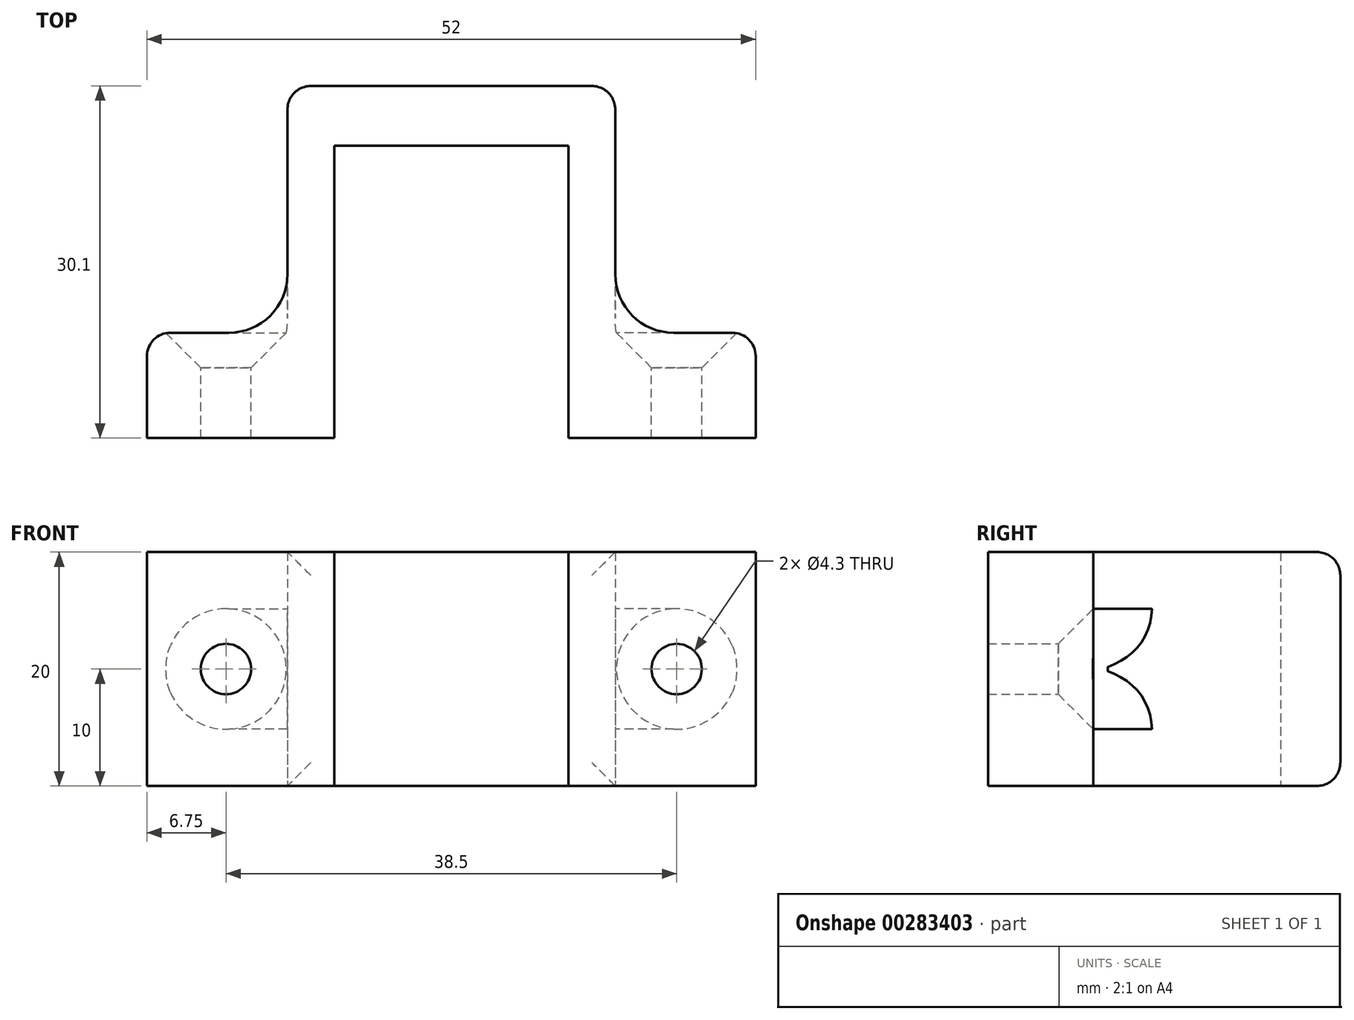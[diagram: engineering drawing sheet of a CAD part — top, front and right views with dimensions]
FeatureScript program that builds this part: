
annotation { "Feature Type Name" : "Feature", "Feature Type Description" : "" }
export const myFeature = defineFeature(function(context is Context, id is Id, definition is map)
    precondition{}
    {
        {
            var Q0;
            Q0=qCreatedBy(makeId("Top.planeOp"),FACE);
            var sketch = newSketch(context, id + "F0", { "sketchPlane" : qUnion([Q0])});
            skLineSegment(sketch, "E0.bottom", {"start": v(14, 12.55) * mm, "end": v(-14, 12.55) * mm});
            skLineSegment(sketch, "E0.top", {"start": v(26, -12.55) * mm, "end": v(10, -12.55) * mm});
            skLineSegment(sketch, "E0.left", {"start": v(26, -8.55) * mm, "end": v(26, -12.55) * mm});
            skLineSegment(sketch, "E0.right", {"start": v(-26, -8.55) * mm, "end": v(-26, -12.55) * mm});
            skPoint(sketch, "E0.middle", {"position": v(0, 0) * mm});
            skLineSegment(sketch, "E1.top", {"start": v(-26, -8.55) * mm, "end": v(-14, -8.55) * mm});
            skLineSegment(sketch, "E1.right", {"start": v(-14, 12.55) * mm, "end": v(-14, -8.55) * mm});
            skLineSegment(sketch, "E2.top", {"start": v(26, -8.55) * mm, "end": v(14, -8.55) * mm});
            skLineSegment(sketch, "E2.right", {"start": v(14, 12.55) * mm, "end": v(14, -8.55) * mm});
            skLineSegment(sketch, "E3.top", {"start": v(-10, 7.45) * mm, "end": v(10, 7.45) * mm});
            skLineSegment(sketch, "E3.left", {"start": v(-10, -12.55) * mm, "end": v(-10, 7.45) * mm});
            skLineSegment(sketch, "E3.right", {"start": v(10, -12.55) * mm, "end": v(10, 7.45) * mm});
            skPoint(sketch, "E4.orphan", {"position": v(-26, 12.55) * mm});
            skPoint(sketch, "E5.orphan", {"position": v(26, 12.55) * mm});
            skLineSegment(sketch, "E6.trimOffspring", {"start": v(-10, -12.55) * mm, "end": v(-26, -12.55) * mm});
            skSolve(sketch);
        }
        {
            var Q0;
            Q0 = qSketchRegion(id + "F0", true);
            extrude(context, id + "F1", {"entities" : qUnion([Q0]), "depth" : 20 * mm});
        }
        {
            var Q0;
            Q0=qCreatedBy(makeId("Front.planeOp"),FACE);
            var sketch = newSketch(context, id + "F2", { "sketchPlane" : qUnion([Q0])});
            skCircle(sketch, "E7", {"center": v(-19.25, 10) * mm, "radius": 2.15 * mm});
            skCircle(sketch, "E8", {"center": v(19.25, 10) * mm, "radius": 2.15 * mm});
            skSolve(sketch);
        }
        {
            var Q0;
            Q0 = qSketchRegion(id + "F2", true);
            extrude(context, id + "F3", {"entities" : qUnion([Q0]), "operationType" : NewBodyOperationType.REMOVE, "depth" : 25 * mm});
        }
        {
            var Q0;
            Q0=makeQuery(id+"F3.boolean.opBoolean","INTERSECT",EDGE,{"derivedFrom":[makeQuery(id+"F1.opExtrude","SWEPT_FACE",FACE,{"disambiguationData":[OSD([sQuery(id+"F0.wireOp",EDGE,"E1.top")])]}),makeQuery(id+"F3.opExtrude","SWEPT_FACE",FACE,{"disambiguationData":[OSD([sQuery(id+"F2.wireOp",EDGE,"E7")])]})]});
            chamfer(context, id + "F4", {"entities" : qUnion([Q0]), "width" : 3 * mm, "tangentPropagation" : true});
        }
        {
            var Q0;
            Q0=makeQuery(id+"F3.boolean.opBoolean","INTERSECT",EDGE,{"derivedFrom":[makeQuery(id+"F1.opExtrude","SWEPT_FACE",FACE,{"disambiguationData":[OSD([sQuery(id+"F0.wireOp",EDGE,"E2.top")])]}),makeQuery(id+"F3.opExtrude","SWEPT_FACE",FACE,{"disambiguationData":[OSD([sQuery(id+"F2.wireOp",EDGE,"E8")])]})]});
            chamfer(context, id + "F5", {"entities" : qUnion([Q0]), "width" : 3 * mm, "tangentPropagation" : true});
        }
        {
            var Q0;
            Q0=makeQuery(id+"F1.opExtrude","SWEPT_EDGE",EDGE,{"disambiguationData":[OSD([sQuery(id+"F0.wireOp",EDGE,"E2.top"),sQuery(id+"F0.wireOp",EDGE,"E2.right")])]});
            var Q1;
            Q1=makeQuery(id+"F1.opExtrude","SWEPT_EDGE",EDGE,{"disambiguationData":[OSD([sQuery(id+"F0.wireOp",EDGE,"E1.top"),sQuery(id+"F0.wireOp",EDGE,"E1.right")])]});
            fillet(context, id + "F6", {"entities" : qUnion([Q0, Q1]), "radius" : 5 * mm, "tangentPropagation" : true, "allowEdgeOverflow" : false});
        }
        {
            var Q0;
            Q0=makeQuery(id+"F1.opExtrude","SWEPT_EDGE",EDGE,{"disambiguationData":[OSD([sQuery(id+"F0.wireOp",EDGE,"E0.left"),sQuery(id+"F0.wireOp",EDGE,"E2.top")])]});
            var Q1;
            Q1=makeQuery(id+"F1.opExtrude","SWEPT_EDGE",EDGE,{"disambiguationData":[OSD([sQuery(id+"F0.wireOp",EDGE,"E0.bottom"),sQuery(id+"F0.wireOp",EDGE,"E2.right")])]});
            var Q2;
            Q2=makeQuery(id+"F1.opExtrude","CAP_EDGE",EDGE,{"disambiguationData":[OSD([sQuery(id+"F0.wireOp",EDGE,"E0.bottom")])],"isStart":true});
            var Q3;
            Q3=makeQuery(id+"F1.opExtrude","CAP_EDGE",EDGE,{"disambiguationData":[OSD([sQuery(id+"F0.wireOp",EDGE,"E0.bottom")])],"isStart":false});
            var Q4;
            Q4=makeQuery(id+"F1.opExtrude","SWEPT_EDGE",EDGE,{"disambiguationData":[OSD([sQuery(id+"F0.wireOp",EDGE,"E0.bottom"),sQuery(id+"F0.wireOp",EDGE,"E1.right")])]});
            var Q5;
            Q5=makeQuery(id+"F1.opExtrude","SWEPT_EDGE",EDGE,{"disambiguationData":[OSD([sQuery(id+"F0.wireOp",EDGE,"E0.right"),sQuery(id+"F0.wireOp",EDGE,"E1.top")])]});
            fillet(context, id + "F7", {"entities" : qUnion([Q0, Q1, Q2, Q3, Q4, Q5]), "radius" : 2 * mm, "tangentPropagation" : true, "allowEdgeOverflow" : false});
        }
        {
            var Q0;
            Q0=makeQuery(id+"F1.opExtrude","SWEPT_FACE",FACE,{"disambiguationData":[OSD([sQuery(id+"F0.wireOp",EDGE,"E0.top")])]});
            var Q1;
            Q1=makeQuery(id+"F1.opExtrude","SWEPT_FACE",FACE,{"disambiguationData":[OSD([sQuery(id+"F0.wireOp",EDGE,"E6.trimOffspring")])]});
            extrude(context, id + "F8", {"entities" : qUnion([Q0, Q1]), "operationType" : NewBodyOperationType.ADD, "depth" : 5 * mm});
        }
    });
